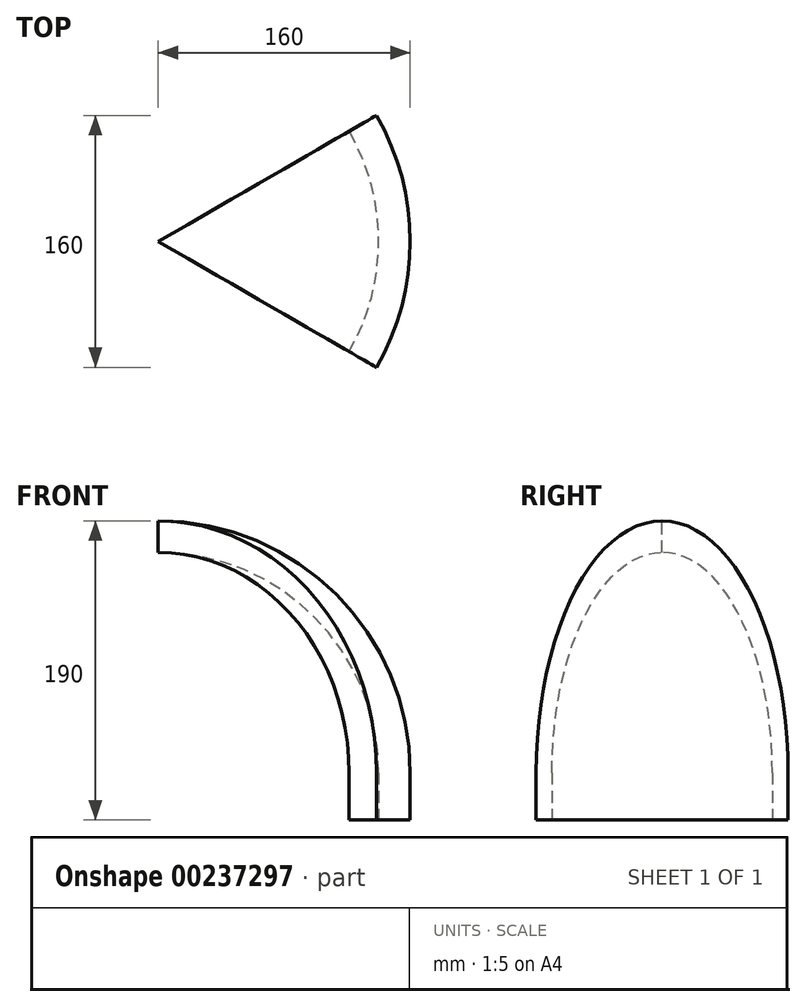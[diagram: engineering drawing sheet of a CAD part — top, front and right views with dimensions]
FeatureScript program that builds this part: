
annotation { "Feature Type Name" : "Feature", "Feature Type Description" : "" }
export const myFeature = defineFeature(function(context is Context, id is Id, definition is map)
    precondition{}
    {
        {
            var Q0;
            Q0=qCreatedBy(makeId("Front.planeOp"),FACE);
            var sketch = newSketch(context, id + "F0", { "sketchPlane" : qUnion([Q0])});
            skLineSegment(sketch, "E0", {"start": v(0, 0) * mm, "end": v(0, 100) * mm, "construction": true});
            skSolve(sketch);
        }
        {
            var Q0;
            Q0=qCreatedBy(makeId("Front.planeOp"),FACE);
            var sketch = newSketch(context, id + "F1", { "sketchPlane" : qUnion([Q0])});
            skArc(sketch, "E1", {"start": v(140, 0) * mm, "mid": v(99, 99) * mm, "end": v(0, 140) * mm});
            skArc(sketch, "E2", {"start": v(160, 0) * mm, "mid": v(113.14, 113.14) * mm, "end": v(0, 160) * mm});
            skLineSegment(sketch, "E3", {"start": v(140, 0) * mm, "end": v(140, -30) * mm});
            skLineSegment(sketch, "E4", {"start": v(140, -30) * mm, "end": v(160, -30) * mm});
            skLineSegment(sketch, "E5", {"start": v(160, -30) * mm, "end": v(160, 0) * mm});
            skLineSegment(sketch, "E6", {"start": v(0, 140) * mm, "end": v(0, 160) * mm});
            skLineSegment(sketch, "E7", {"start": v(0, 0) * mm, "end": v(140, 0) * mm, "construction": true});
            skLineSegment(sketch, "E8", {"start": v(0, 0) * mm, "end": v(99, 99) * mm, "construction": true});
            skSolve(sketch);
        }
        {
            var Q0;
            Q0=makeQuery(id+"F1.imprint","IMPRINT",FACE,{"disambiguationData":[TD([[makeQuery(id+"F1.imprint","IMPRINT",EDGE,{"derivedFrom":sQuery(id+"F1.wireOp",EDGE,"E1")}),-1.0]])]});
            var Q1;
            Q1=sQuery(id+"F0.wireOp",EDGE,"E0");
            revolve(context, id + "F2", {"entities" : qUnion([Q0]), "axis" : qUnion([Q1]), "revolveType" : RevolveType.TWO_DIRECTIONS, "angle" : 30 * degree, "angleBack" : 330 * degree});
        }
    });
